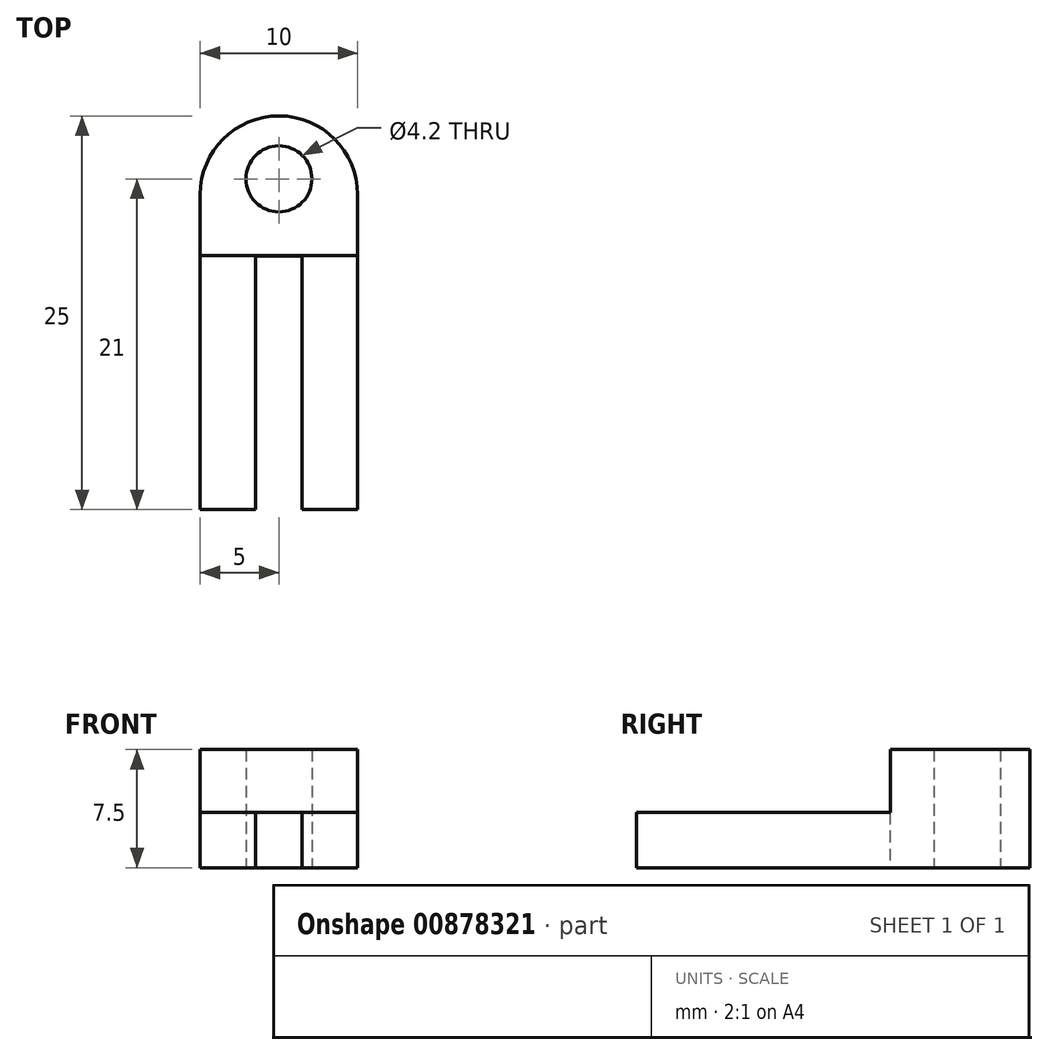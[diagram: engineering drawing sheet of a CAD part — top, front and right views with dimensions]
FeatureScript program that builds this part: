
annotation { "Feature Type Name" : "Feature", "Feature Type Description" : "" }
export const myFeature = defineFeature(function(context is Context, id is Id, definition is map)
    precondition{}
    {
        {
            var Q0;
            Q0=qCreatedBy(makeId("Top.planeOp"),FACE);
            var sketch = newSketch(context, id + "F0", { "sketchPlane" : qUnion([Q0])});
            skLineSegment(sketch, "E0.bottom", {"start": v(5, -12.5) * mm, "end": v(1.48, -12.5) * mm});
            skLineSegment(sketch, "E0.top", {"start": v(5, 12.5) * mm, "end": v(-5, 12.5) * mm});
            skLineSegment(sketch, "E0.left", {"start": v(5, -12.5) * mm, "end": v(5, 12.5) * mm});
            skLineSegment(sketch, "E0.right", {"start": v(-5, -12.5) * mm, "end": v(-5, 12.5) * mm});
            skPoint(sketch, "E0.middle", {"position": v(0, 0) * mm});
            skCircle(sketch, "E1", {"center": v(0, 8.5) * mm, "radius": 2.1 * mm});
            skLineSegment(sketch, "E2.bottom", {"start": v(-1.49, 3.6) * mm, "end": v(1.48, 3.6) * mm});
            skLineSegment(sketch, "E2.left", {"start": v(-1.49, 3.6) * mm, "end": v(-1.49, -12.5) * mm});
            skLineSegment(sketch, "E2.right", {"start": v(1.48, 3.6) * mm, "end": v(1.48, -12.5) * mm});
            skLineSegment(sketch, "E3.trimOffspring", {"start": v(-1.49, -12.5) * mm, "end": v(-5, -12.5) * mm});
            skSolve(sketch);
        }
        {
            var Q0;
            Q0=makeQuery(id+"F0.imprint","IMPRINT",FACE,{"disambiguationData":[TD([[makeQuery(id+"F0.imprint","IMPRINT",EDGE,{"derivedFrom":sQuery(id+"F0.wireOp",EDGE,"E0.bottom")}),-1.0]])]});
            extrude(context, id + "F1", {"entities" : qUnion([Q0]), "depth" : 3.5 * mm, "offsetDistance" : 25 * mm});
        }
        {
            var Q0;
            Q0=makeQuery(id+"F1.opExtrude","SWEPT_EDGE",EDGE,{"disambiguationData":[OSD([sQuery(id+"F0.wireOp",EDGE,"E0.top"),sQuery(id+"F0.wireOp",EDGE,"E0.right")])]});
            var Q1;
            Q1=makeQuery(id+"F1.opExtrude","SWEPT_EDGE",EDGE,{"disambiguationData":[OSD([sQuery(id+"F0.wireOp",EDGE,"E0.top"),sQuery(id+"F0.wireOp",EDGE,"E0.left")])]});
            fillet(context, id + "F2", {"entities" : qUnion([Q0, Q1]), "radius" : 5 * mm, "tangentPropagation" : true, "allowEdgeOverflow" : false});
        }
        {
            var Q0;
            Q0=makeQuery(id+"F1.opExtrude","CAP_FACE",FACE,{"disambiguationData":[OSD([sQuery(id+"F0.wireOp",EDGE,"E0.bottom"),sQuery(id+"F0.wireOp",EDGE,"E0.top"),sQuery(id+"F0.wireOp",EDGE,"E0.left"),sQuery(id+"F0.wireOp",EDGE,"E0.right"),sQuery(id+"F0.wireOp",EDGE,"E1"),sQuery(id+"F0.wireOp",EDGE,"E2.bottom"),sQuery(id+"F0.wireOp",EDGE,"E2.left"),sQuery(id+"F0.wireOp",EDGE,"E2.right"),sQuery(id+"F0.wireOp",EDGE,"E3.trimOffspring")])],"isStart":false});
            var Q1;
            Q1=makeQuery(id+"F1.opExtrude","CAP_FACE",FACE,{"disambiguationData":[OSD([sQuery(id+"F0.wireOp",EDGE,"E0.bottom"),sQuery(id+"F0.wireOp",EDGE,"E0.top"),sQuery(id+"F0.wireOp",EDGE,"E0.left"),sQuery(id+"F0.wireOp",EDGE,"E0.right"),sQuery(id+"F0.wireOp",EDGE,"E1"),sQuery(id+"F0.wireOp",EDGE,"E2.bottom"),sQuery(id+"F0.wireOp",EDGE,"E2.left"),sQuery(id+"F0.wireOp",EDGE,"E2.right"),sQuery(id+"F0.wireOp",EDGE,"E3.trimOffspring")])],"isStart":false});
            var sketch = newSketch(context, id + "F3", { "sketchPlane" : qUnion([Q0, Q1])});
            skLineSegment(sketch, "E4", {"start": v(0, 3.62) * mm, "end": v(5.03, 3.62) * mm});
            skLineSegment(sketch, "E5", {"start": v(0, 3.62) * mm, "end": v(-5, 3.62) * mm});
            skSolve(sketch);
        }
        {
            var Q0;
            {var subQ5=sQuery(id+"F3.wireOp",EDGE,"E5");Q0=makeQuery(id+"F3.imprint","IMPRINT",FACE,{"disambiguationData":[TD([[makeQuery(id+"F3.imprint","IMPRINT",EDGE,{"derivedFrom":subQ5}),-1.0]])]});}
            extrude(context, id + "F4", {"entities" : qUnion([Q0]), "operationType" : NewBodyOperationType.ADD, "depth" : 4 * mm, "offsetDistance" : 25 * mm});
        }
    });
